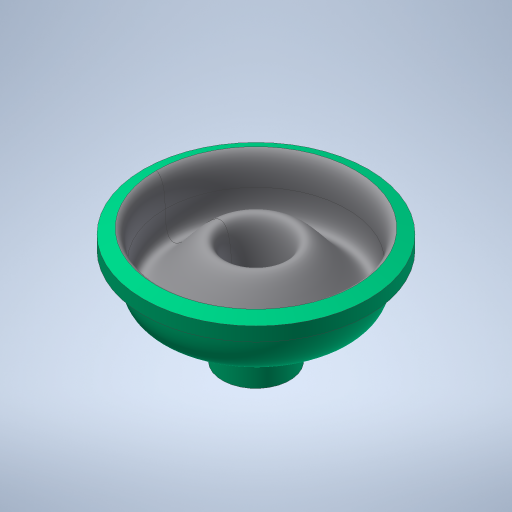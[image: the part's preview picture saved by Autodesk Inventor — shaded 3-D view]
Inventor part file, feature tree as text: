
AUTODESK INVENTOR PART (.ipt)
format: ipt  version: 2023.3 (Build 273359000, 359)  size: 728,064 bytes
history: native  units: mm
features: other x6, sketch x3, surface_op x3, revolve x1, plane x1
ambient origin geometry x8: Origin, YZ Plane, XZ Plane, XY Plane, X Axis, Y Axis, Z Axis, Center Point
bodies: Solid1 (feature_tree)
feature tree (14):
  sketch  "Sketch1"  dims[d3=7.5mm d5=5.0mm]
  revolve  "Revolution1"  [1 undecoded]
  other  "Work Axis1"
  plane  "Work Plane1"
  surface_op  "Stitch Surface2"
  sketch  "Sketch2"  dims[d6=17.453293mm]
  other  "Srf7"
  other  "Srf8"
  sketch  "Sketch4"  dims[d8=360.0deg d29=31.0mm d32=10.5mm d34=2.0mm d35=0.845184mm d36=2.0mm d42=2.0mm d48=15.0mm d52=0.5mm d53=0.5mm d54=45.0deg d55=1.0mm d58=0.0mm d59=0.0mm d60=5.0mm d61=0.0mm d62=5.0mm d63=0.0mm d64=9.0mm d65=3.959262mm d66=1.466951mm]
  other  "Srf9"
  other  "Srf10"
  other  "OffsetSrf2"
  surface_op  "Boundary Patch5"
  surface_op  "Boundary Patch6"
note: 1 required parameter value undecoded (feature->parameter linkage not recoverable at this tier; creation-order binding heuristic only, values carry confidence <= 0.55)
